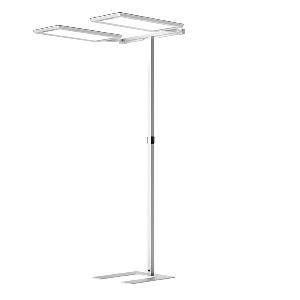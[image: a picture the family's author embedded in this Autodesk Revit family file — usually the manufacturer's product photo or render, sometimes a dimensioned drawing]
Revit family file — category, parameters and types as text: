
# Revit family: yara_doubleu_-_yus_2_15000_vtl_r_sr_cee_s0_c_114268000-00812374_42c0
name_source: partatom
category: Lighting Fixtures
units: mm (PartAtom-declared; Revit-internal decimal feet)

## family parameters
Cut with Voids When Loaded = No
Host = Face
Light Source = No
Part Type = Normal
Room Calculation Point = No
Round Connector Dimension = Use Diameter
Shared = No

## types (1)
- YARA.doubleU - YUS 2/15000/VTL/R/SR/CEE/S0/C (1 x LED, 15000 lm, VTL)
    Apparent Load = 214 VA
    Approval mark = CE
    CIE Flux Codes = 58 87 97 13 100
    Color Rendering = 80-89
    Color Temperature = VTL
    Control Gear = Electronic ballast
    Default Elevation = 1800 mm
    Description = YUS 2/15000/VTL/R/SR/CEE/S0/C|Free-standing luminaire|light source: LED Cold white   |work equipment: Electronic ballast DALI|connected load: 220-240V, 50/60Hz|Power consumption: approx. 210 W|power factor: approx. 0,966|luminous flux: 30000 lm|luminous efficacy: 142 lm/W|light distribution: Direct/indirect|direct ratio: approx. 13 %|color rendering index (CRI): >= 80|chromaticity tolerance:  3 SDCM|technology: Presence and daylight sensor control (PIR)|operation: Wireless switch|luminaire body|material: Aluminium/plastic|surface: Powder coatet|colour: Silver metallic|lamp cover: Acrylic (PMMA)|tubular section|material: Steel tube|surface: Powder-coated|Form: Tubular section upright|colour of tubular section: Silver metallic|luminaire base|Form: C-form flat|weight (net): approx. 26.0 kg|mains lead: 3.00 m Mains plug CEE 7/VII|Fastening: Floor standing base|glare control: Conical prismatic screen|luminance(L65): <= 2700 cd/m|unified glare rating(4H 8H): <=  16|special features: App control, Asymmetric radiation, Biodynamic light VTL, Direct and indirect lighting component with edge light and light guidetechnology for a homogeneous light exit, Flicker-free, Magnetic control panel, freely positionable, PIR movement and daylight sensor, TALK Bluetooth|Approval mark: VDE - ENEC|
    Frequency = 50 Hz, 60 Hz
    Height = 24 mm  [stored 0.0787402 ft]
    Lamp = 1 x LED
    Lamp Light Flux = 15000 lm
    Lamp count = 1
    Length = 690 mm
    Luminous efficacy = 140 lm/W
    Manufacturer = Waldmann
    ModVariant = No
    Model = 114268000-00812374
    Mounting Place = Floor
    Mounting Type = Freestanding
    Number of Poles = 1
    OnlyDefault = Yes
    Power Factor = 1
    Product Name = YARA.doubleU - YUS 2/15000/VTL/R/SR/CEE/S0/C
    Product group = Free standing luminaire
    ProductGroupID = 13
    Protection Class = Protection class I
    Protection Degree = IP 20
    RLX_Detail_Level = 1
    RlxData = <blob elided: 68621 chars, md5=1695a4ff>
    Socket = socket
    Standby Power = 0 W
    System Light Flux = 30000 lm
    System Power = 214 W
    Type Comments = Product without accessories
    Type Image = yus-r-sr-c.jpg
    URL = http://relux.com
    VarID = ---
    Voltage = 230 V
    Voltage Range = 220-240 V
    Weight = 0.00 kg
    Width = 358 mm

note: [stored X ft] marks values corroborated as IEEE doubles in the binary element streams (Revit-internal decimal feet)

## geometry (parser evidence)
native form markers: Blend x4, Sweep x21
no freeform markers — native parametric forms only
